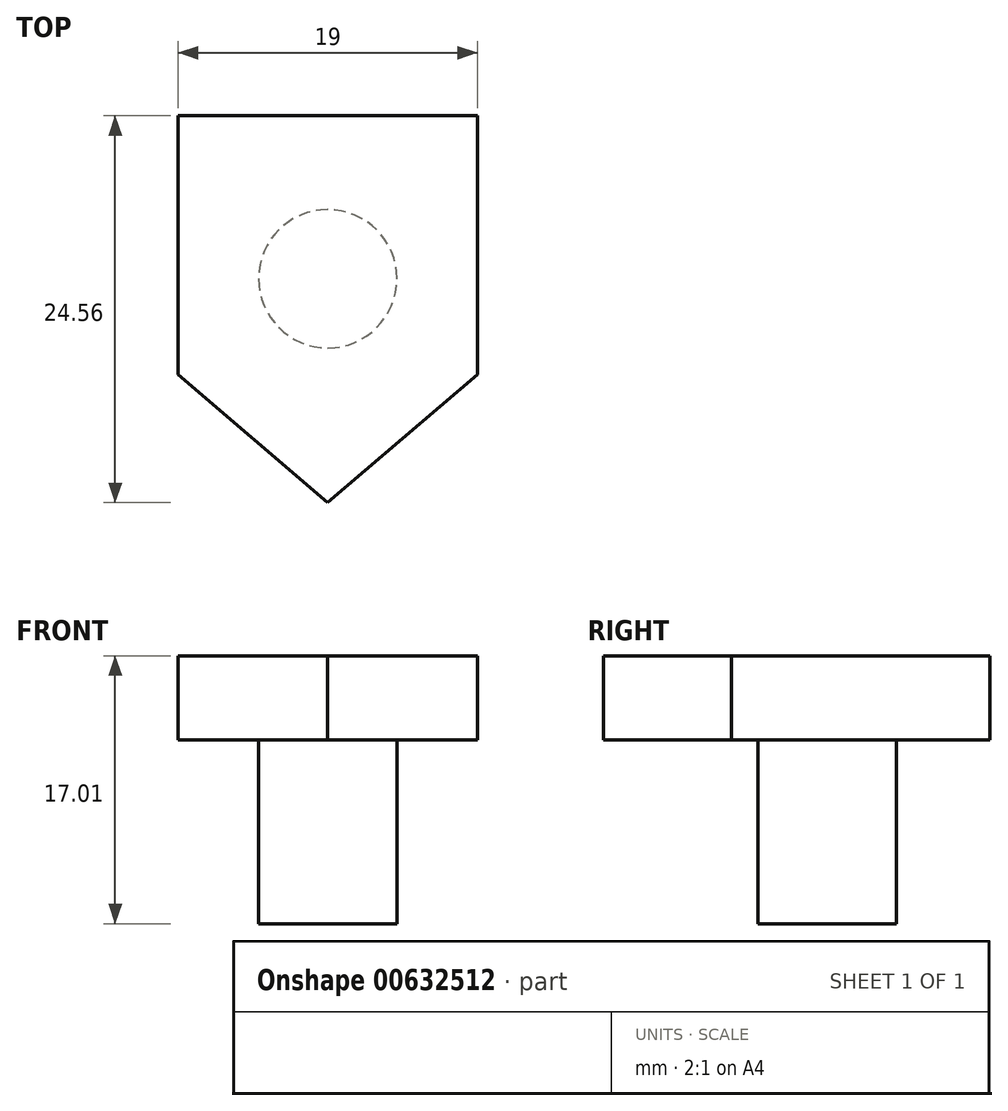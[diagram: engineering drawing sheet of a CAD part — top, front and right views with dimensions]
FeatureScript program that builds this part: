
annotation { "Feature Type Name" : "Feature", "Feature Type Description" : "" }
export const myFeature = defineFeature(function(context is Context, id is Id, definition is map)
    precondition{}
    {
        {
            var Q0;
            Q0=qCreatedBy(makeId("Top.planeOp"),FACE);
            var sketch = newSketch(context, id + "F0", { "sketchPlane" : qUnion([Q0])});
            skLineSegment(sketch, "E0", {"start": v(-50.08, 30.8) * mm, "end": v(-50.08, 47.23) * mm});
            skLineSegment(sketch, "E1", {"start": v(-50.08, 47.23) * mm, "end": v(-31.08, 47.23) * mm});
            skLineSegment(sketch, "E2", {"start": v(-31.08, 47.23) * mm, "end": v(-31.08, 30.8) * mm});
            skLineSegment(sketch, "E3", {"start": v(-31.08, 30.8) * mm, "end": v(-40.58, 22.67) * mm});
            skPoint(sketch, "E3.endSnap0", {"position": v(-40.58, 47.23) * mm});
            skLineSegment(sketch, "E4", {"start": v(-40.58, 22.67) * mm, "end": v(-50.08, 30.8) * mm});
            skSolve(sketch);
        }
        {
            var Q0;
            Q0 = qSketchRegion(id + "F0", true);
            extrude(context, id + "F1", {"entities" : qUnion([Q0]), "depth" : 5.33 * mm, "offsetDistance" : 25.4 * mm});
        }
        {
            var Q0;
            Q0=makeQuery(id+"F1.opExtrude","CAP_FACE",FACE,{"disambiguationData":[OSD([sQuery(id+"F0.wireOp",EDGE,"E0"),sQuery(id+"F0.wireOp",EDGE,"E1"),sQuery(id+"F0.wireOp",EDGE,"E2"),sQuery(id+"F0.wireOp",EDGE,"E3"),sQuery(id+"F0.wireOp",EDGE,"E4")])],"isStart":false});
            var sketch = newSketch(context, id + "F2", { "sketchPlane" : qUnion([Q0])});
            skCircle(sketch, "E5", {"center": v(-40.58, 36.88) * mm, "radius": 4.4 * mm});
            skSolve(sketch);
        }
        {
            var Q0;
            Q0 = qSketchRegion(id + "F2", true);
            extrude(context, id + "F3", {"entities" : qUnion([Q0]), "operationType" : NewBodyOperationType.ADD, "oppositeDirection" : true, "depth" : 17.02 * mm, "offsetDistance" : 25.4 * mm});
        }
    });
